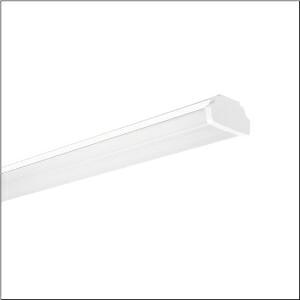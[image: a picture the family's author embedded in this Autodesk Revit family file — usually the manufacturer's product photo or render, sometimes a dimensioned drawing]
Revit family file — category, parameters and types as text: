
# Revit family: modario_r__31_mo_53bm81271v6080_691a
name_source: partatom
category: Lighting Fixtures
units: mm (PartAtom-declared; Revit-internal decimal feet)

## family parameters
Cut with Voids When Loaded = No
Host = Face
Light Source = No
Part Type = Normal
Room Calculation Point = No
Round Connector Dimension = Use Diameter
Shared = No

## types (1)
- Modario® 31 MO (1 x LED, 7820 lm, 50.8 W, 6500K)
    Apparent Load = 51 VA
    CIE Flux Codes = 47 80 95 92 100
    Color Rendering = 80
    Color Temperature = 6500K
    Default Elevation = 1800 mm
    Description = Modario® 31 MO, luminaire insert, of sheet steel, coil coated, white, length: 1.495mm, width: 81mm, height: 82mm, 5x system unit, system units: 299mm, LED rated luminous flux: 7.820lm, light colour: 865, control gear: ON/OFF, control gear: ECG, with plug, 3-pole, with phase selection, mains connection: 220..240V, AC, 50/60Hz, rated input power: 51W, through-wiring accessed according to module size, primary optical cover: cover, of PMMA, light emission: direct distribution, primary light characteristic: symmetric, protection rating (complete): IP20, protection rating (LED compartment): IP50, insulation class (complete): insulation class I (protective earthing), certification: CE, ENEC, VDE, UKCA, impact resistance: IK03, permissible ambient temperature for indoor applications: -35..+35°C, corresponds to IFS (International Featured Standards) requirements for safety and quality in the food industry, reducing of maximum allowable ambient temperature of 5°C with ceiling mounting, packaging unit: 1 piece
    Height = 92 mm
    Lamp = 1 x LED
    Lamp Light Flux = 7820 lm
    Lamp Power = 50.8 W
    Lamp count = 1
    Length = 1495 mm
    Luminous efficacy = 154 lm/W
    Manufacturer = Siteco
    ModVariant = No
    Model = 53BM81271V6080
    Mounting Place = Ceiling
    Mounting Type = Pendant
    Number of Poles = 1
    OnlyDefault = Yes
    Power Factor = 1
    Product Name = Modario® 31 MO
    Product group = luminaire insert
    ProductGroupID = 901
    Protection Class = Protection class I
    Protection Degree = IP 20
    RLX_Detail_Level = 1
    RLX_Emergency_Light_Flux = 0 lm
    RLX_Emergency_Type = 0
    RLX_Emergency_Type_DB = No
    RlxData = <blob elided: 38765 chars, md5=2220b070>
    Socket = socket
    Standby Power = 0 W
    System Light Flux = 7820 lm
    System Power = 51 W
    Type Comments = Product without accessories
    Type Image = l_1300283.jpg
    URL = http://relux.com
    VarID = ---
    Voltage = 0 V
    Weight = 0.00 kg
    Width = 81 mm

## geometry (parser evidence)
native form markers: Blend x4, Sweep x11
no freeform markers — native parametric forms only
